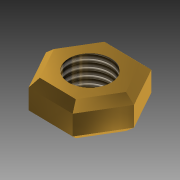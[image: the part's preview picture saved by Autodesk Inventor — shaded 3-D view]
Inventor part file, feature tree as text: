
AUTODESK INVENTOR PART (.ipt)
format: ipt  version: 2015 (Build 190159000, 159)  size: 123,904 bytes
history: native  units: mm
features: extrude x2, sketch x2, other x1, thread x1, chamfer x1
ambient origin geometry x8: Origin, YZ Plane, XZ Plane, XY Plane, X Axis, Y Axis, Z Axis, Center Point
bodies: Body1 (feature_tree)
feature tree (7):
  other  "ソリッド1"
  extrude  "押し出し1"  Depth=5.5mm
  extrude  "押し出し2"  Depth=2.4mm TaperAngle=0.0deg
  thread  "ねじ1"
  chamfer  "面取り1"  Distance=3.0mm
  sketch  "スケッチ1"
  sketch  "スケッチ2"
